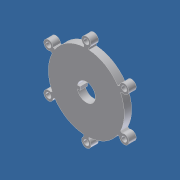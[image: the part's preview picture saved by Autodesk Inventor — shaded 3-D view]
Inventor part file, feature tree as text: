
AUTODESK INVENTOR PART (.ipt)
format: ipt  version: unknown  size: 235,520 bytes
history: native  units: in
note: dims shown in document units (in); Inventor stores cm internally (conversion verified against a paired STEP export)
features: extrude x1, sketch x1
ambient origin geometry x8: Origin, YZ Plane, XZ Plane, XY Plane, X Axis, Y Axis, Z Axis, Center Point
feature tree (2):
  extrude  "Extrusion3"  Depth=0.376in
  sketch  "Sketch1"  dims[d0=1.625in d6=0.376in d30=0.157in d31=0.0in]
